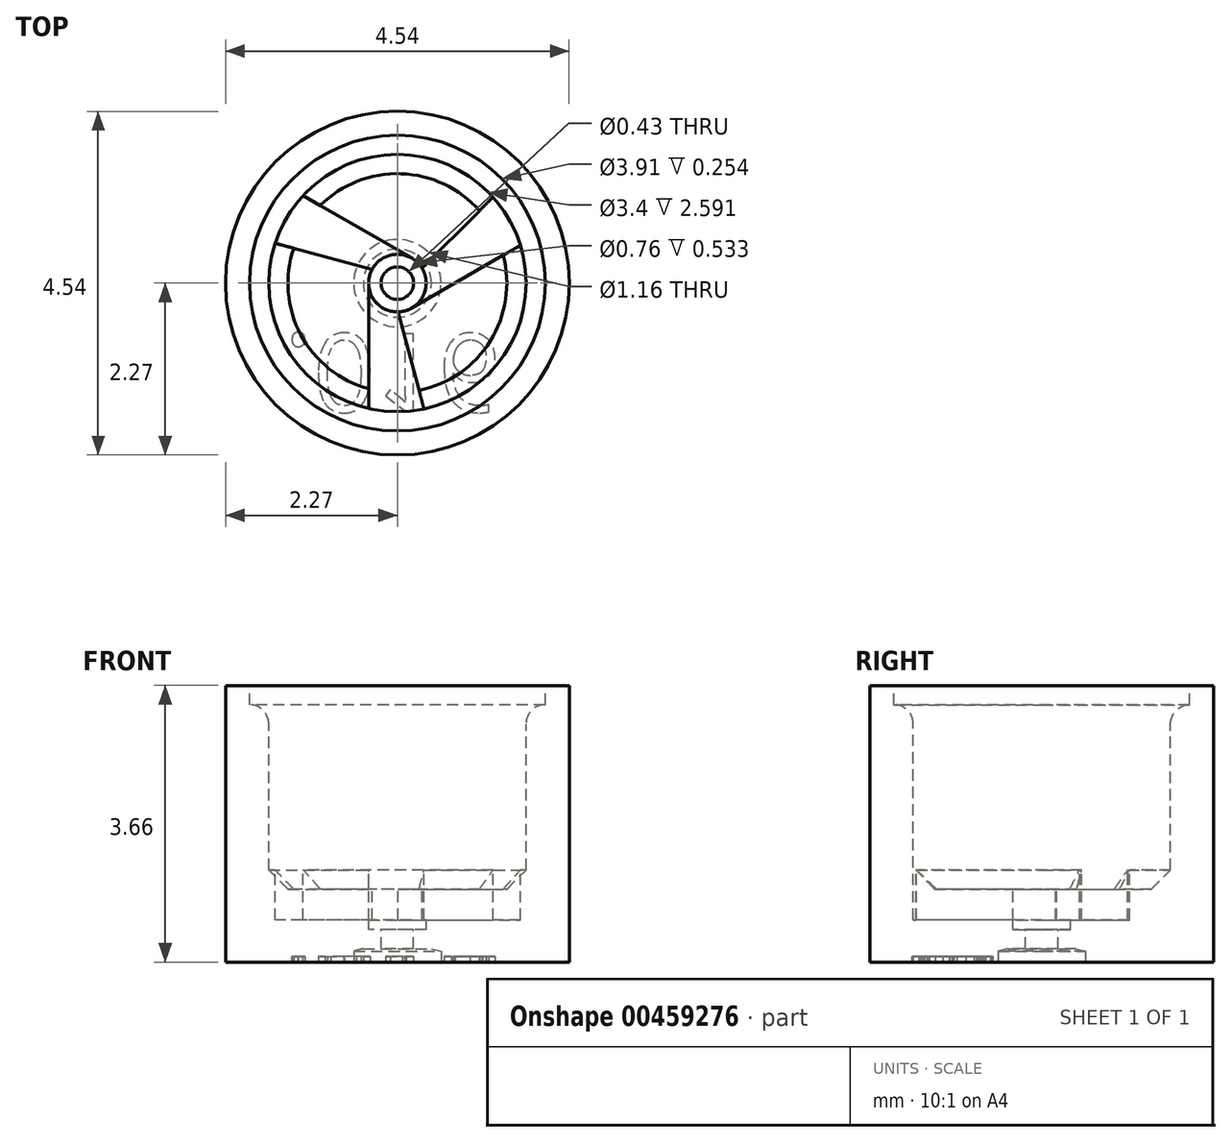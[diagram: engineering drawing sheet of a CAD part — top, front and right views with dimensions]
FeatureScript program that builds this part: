
annotation { "Feature Type Name" : "Feature", "Feature Type Description" : "" }
export const myFeature = defineFeature(function(context is Context, id is Id, definition is map)
    precondition{}
    {
        {
            var Q0;
            Q0=qCreatedBy(makeId("Top.planeOp"),FACE);
            var sketch = newSketch(context, id + "F0", { "sketchPlane" : qUnion([Q0])});
            skCircle(sketch, "E0", {"center": v(0, 0) * mm, "radius": 2.27 * mm});
            skSolve(sketch);
        }
        {
            var Q0;
            Q0=qSketchRegion(id+"F0",true);
            extrude(context, id + "F1", {"entities" : qUnion([Q0]), "depth" : 3.66 * mm});
        }
        {
            var Q0;
            Q0=makeQuery(id+"F1.opExtrude","CAP_FACE",FACE,{"disambiguationData":[OSD([sQuery(id+"F0.wireOp",EDGE,"E0")])],"isStart":false});
            var sketch = newSketch(context, id + "F2", { "sketchPlane" : qUnion([Q0])});
            skCircle(sketch, "E1", {"center": v(0, 0) * mm, "radius": 1.96 * mm});
            skSolve(sketch);
        }
        {
            var Q0;
            Q0=makeQuery(id+"F2.imprint","IMPRINT",FACE,{"disambiguationData":[TD([[makeQuery(id+"F2.imprint","IMPRINT",EDGE,{"derivedFrom":sQuery(id+"F2.wireOp",EDGE,"E1")}),1.0]])]});
            extrude(context, id + "F3", {"entities" : qUnion([Q0]), "operationType" : NewBodyOperationType.REMOVE, "oppositeDirection" : true, "depth" : 0.25 * mm});
        }
        {
            var Q0;
            Q0=makeQuery(id+"F3.boolean.opBoolean","COPY",FACE,{"derivedFrom":makeQuery(id+"F3.opExtrude","CAP_FACE",FACE,{"disambiguationData":[OSD([sQuery(id+"F2.wireOp",EDGE,"E1")])],"isStart":false})});
            var sketch = newSketch(context, id + "F4", { "sketchPlane" : qUnion([Q0])});
            skCircle(sketch, "E2", {"center": v(0, 0) * mm, "radius": 1.7 * mm});
            skSolve(sketch);
        }
        {
            var Q0;
            Q0=makeQuery(id+"F4.imprint","IMPRINT",FACE,{"disambiguationData":[TD([[makeQuery(id+"F4.imprint","IMPRINT",EDGE,{"derivedFrom":sQuery(id+"F4.wireOp",EDGE,"E2")}),1.0]])]});
            extrude(context, id + "F5", {"entities" : qUnion([Q0]), "operationType" : NewBodyOperationType.REMOVE, "oppositeDirection" : true, "depth" : 2.44 * mm});
        }
        {
            var Q0;
            Q0=makeQuery(id+"F5.boolean.opBoolean","COPY",EDGE,{"derivedFrom":makeQuery(id+"F5.opExtrude","CAP_EDGE",EDGE,{"disambiguationData":[OSD([sQuery(id+"F4.wireOp",EDGE,"E2")])],"isStart":false})});
            chamfer(context, id + "F6", {"entities" : qUnion([Q0]), "chamferType" : ChamferType.OFFSET_ANGLE, "width" : 0.25 * mm, "oppositeDirection" : false, "angle" : 45 * degree, "tangentPropagation" : true});
        }
        {
            var Q0;
            Q0=makeQuery(id+"F5.boolean.opBoolean","COPY",FACE,{"derivedFrom":makeQuery(id+"F5.opExtrude","CAP_FACE",FACE,{"disambiguationData":[OSD([sQuery(id+"F4.wireOp",EDGE,"E2")])],"isStart":false})});
            var sketch = newSketch(context, id + "F7", { "sketchPlane" : qUnion([Q0])});
            skCircle(sketch, "E3", {"center": v(0, 0) * mm, "radius": 0.38 * mm});
            skSolve(sketch);
        }
        {
            var Q0;
            Q0=makeQuery(id+"F7.imprint","IMPRINT",FACE,{"disambiguationData":[TD([[makeQuery(id+"F7.imprint","IMPRINT",EDGE,{"derivedFrom":sQuery(id+"F7.wireOp",EDGE,"E3")}),1.0]])]});
            extrude(context, id + "F8", {"entities" : qUnion([Q0]), "operationType" : NewBodyOperationType.REMOVE, "oppositeDirection" : true, "depth" : 0.53 * mm});
        }
        {
            var Q0;
            Q0=makeQuery(id+"F8.boolean.opBoolean","COPY",FACE,{"derivedFrom":makeQuery(id+"F8.opExtrude","CAP_FACE",FACE,{"disambiguationData":[OSD([sQuery(id+"F7.wireOp",EDGE,"E3")])],"isStart":false})});
            var sketch = newSketch(context, id + "F9", { "sketchPlane" : qUnion([Q0])});
            skCircle(sketch, "E4", {"center": v(0, 0) * mm, "radius": 0.21 * mm});
            skSolve(sketch);
        }
        {
            var Q0;
            Q0=makeQuery(id+"F9.imprint","IMPRINT",FACE,{"disambiguationData":[TD([[makeQuery(id+"F9.imprint","IMPRINT",EDGE,{"derivedFrom":sQuery(id+"F9.wireOp",EDGE,"E4")}),1.0]])]});
            extrude(context, id + "F10", {"entities" : qUnion([Q0]), "operationType" : NewBodyOperationType.REMOVE, "oppositeDirection" : true, "depth" : 25.4 * mm});
        }
        {
            var Q0;
            Q0=makeQuery(id+"F1.opExtrude","CAP_FACE",FACE,{"disambiguationData":[OSD([sQuery(id+"F0.wireOp",EDGE,"E0")])],"isStart":true});
            var sketch = newSketch(context, id + "F11", { "sketchPlane" : qUnion([Q0])});
            skCircle(sketch, "E5", {"center": v(0, 0) * mm, "radius": 0.58 * mm});
            skSolve(sketch);
        }
        {
            var Q0;
            Q0=makeQuery(id+"F11.imprint","IMPRINT",FACE,{"disambiguationData":[TD([[makeQuery(id+"F11.imprint","IMPRINT",EDGE,{"derivedFrom":sQuery(id+"F11.wireOp",EDGE,"E5")}),1.0]])]});
            extrude(context, id + "F12", {"entities" : qUnion([Q0]), "operationType" : NewBodyOperationType.REMOVE, "oppositeDirection" : true, "depth" : 0.18 * mm});
        }
        {
            var Q0;
            Q0=makeQuery(id+"F12.boolean.opBoolean","COPY",EDGE,{"derivedFrom":makeQuery(id+"F12.opExtrude","CAP_EDGE",EDGE,{"disambiguationData":[OSD([sQuery(id+"F11.wireOp",EDGE,"E5")])],"isStart":false})});
            chamfer(context, id + "F13", {"entities" : qUnion([Q0]), "chamferType" : ChamferType.OFFSET_ANGLE, "width" : 0.13 * mm, "oppositeDirection" : false, "angle" : 15 * degree, "tangentPropagation" : true});
        }
        {
            var Q0;
            Q0=makeQuery(id+"F5.boolean.opBoolean","COPY",FACE,{"derivedFrom":makeQuery(id+"F5.opExtrude","CAP_FACE",FACE,{"disambiguationData":[OSD([sQuery(id+"F4.wireOp",EDGE,"E2")])],"isStart":false})});
            var sketch = newSketch(context, id + "F14", { "sketchPlane" : qUnion([Q0])});
            skArc(sketch, "E6.0", {"start": v(0.2, 0.33) * mm, "mid": v(-0.1, 0.37) * mm, "end": v(-0.33, 0.18) * mm});
            skArc(sketch, "E7.0", {"start": v(-1.25, 1.16) * mm, "mid": v(-1.47, 0.86) * mm, "end": v(-1.62, 0.53) * mm});
            skLineSegment(sketch, "E8", {"start": v(0.2, 0.33) * mm, "end": v(-1.25, 1.16) * mm});
            skLineSegment(sketch, "E9", {"start": v(-0.33, 0.18) * mm, "end": v(-1.62, 0.53) * mm});
            skLineSegment(sketch, "E10.1.0", {"start": v(-0.38, 0) * mm, "end": v(-0.38, -1.66) * mm});
            skArc(sketch, "E10.1.1", {"start": v(-0.38, 0) * mm, "mid": v(-0.27, -0.27) * mm, "end": v(0, -0.38) * mm});
            skLineSegment(sketch, "E10.1.2", {"start": v(0, -0.38) * mm, "end": v(0.35, -1.66) * mm});
            skArc(sketch, "E10.1.3", {"start": v(-0.38, -1.66) * mm, "mid": v(-0.01, -1.7) * mm, "end": v(0.35, -1.66) * mm});
            skLineSegment(sketch, "E10.2.0", {"start": v(0.2, -0.33) * mm, "end": v(1.63, 0.5) * mm});
            skArc(sketch, "E10.2.1", {"start": v(0.2, -0.33) * mm, "mid": v(0.37, -0.1) * mm, "end": v(0.33, 0.2) * mm});
            skLineSegment(sketch, "E10.2.2", {"start": v(0.33, 0.2) * mm, "end": v(1.27, 1.14) * mm});
            skArc(sketch, "E10.2.3", {"start": v(1.63, 0.5) * mm, "mid": v(1.48, 0.84) * mm, "end": v(1.27, 1.14) * mm});
            skSolve(sketch);
        }
        {
            var Q0;
            Q0=qSketchRegion(id+"F14",true);
            extrude(context, id + "F15", {"entities" : qUnion([Q0]), "operationType" : NewBodyOperationType.REMOVE, "oppositeDirection" : true, "depth" : 0.4 * mm});
        }
        {
            var Q0;
            Q0=qSketchRegion(id+"F14",true);
            extrude(context, id + "F16", {"entities" : qUnion([Q0]), "operationType" : NewBodyOperationType.REMOVE, "depth" : 25.4 * mm});
        }
        {
            var Q0;
            Q0=makeQuery(id+"F16.boolean.opBoolean","INTERSECT",EDGE,{"derivedFrom":[makeQuery(id+"F16.opExtrude","SWEPT_FACE",FACE,{"disambiguationData":[OSD([sQuery(id+"F14.wireOp",EDGE,"E7.0")])]}),makeQuery(id+"F16.opExtrude","SWEPT_FACE",FACE,{"disambiguationData":[OSD([sQuery(id+"F14.wireOp",EDGE,"E10.1.3")])]}),makeQuery(id+"F16.opExtrude","SWEPT_FACE",FACE,{"disambiguationData":[OSD([sQuery(id+"F14.wireOp",EDGE,"E10.2.3")])]})]});
            fillet(context, id + "F17", {"entities" : qUnion([Q0]), "radius" : 0.25 * mm, "tangentPropagation" : true, "allowEdgeOverflow" : false});
        }
        {
            var Q0;
            Q0=makeQuery(id+"F1.opExtrude","CAP_FACE",FACE,{"disambiguationData":[OSD([sQuery(id+"F0.wireOp",EDGE,"E0")])],"isStart":true});
            var sketch = newSketch(context, id + "F18", { "sketchPlane" : qUnion([Q0])});
            skText(sketch, "E11", { "text": ".016\n", "fontName": "OpenSans-Regular.ttf"});
            const initialGuessF18  = {"E11": [-0.0015, 0.00067, 1, 0, 0.00104]};
            skSetInitialGuess(sketch, initialGuessF18);
            skSolve(sketch);
        }
        {
            var Q0;
            Q0=qSketchRegion(id+"F18",true);
            extrude(context, id + "F19", {"entities" : qUnion([Q0]), "operationType" : NewBodyOperationType.REMOVE, "oppositeDirection" : true, "depth" : 0.08 * mm});
        }
    });
